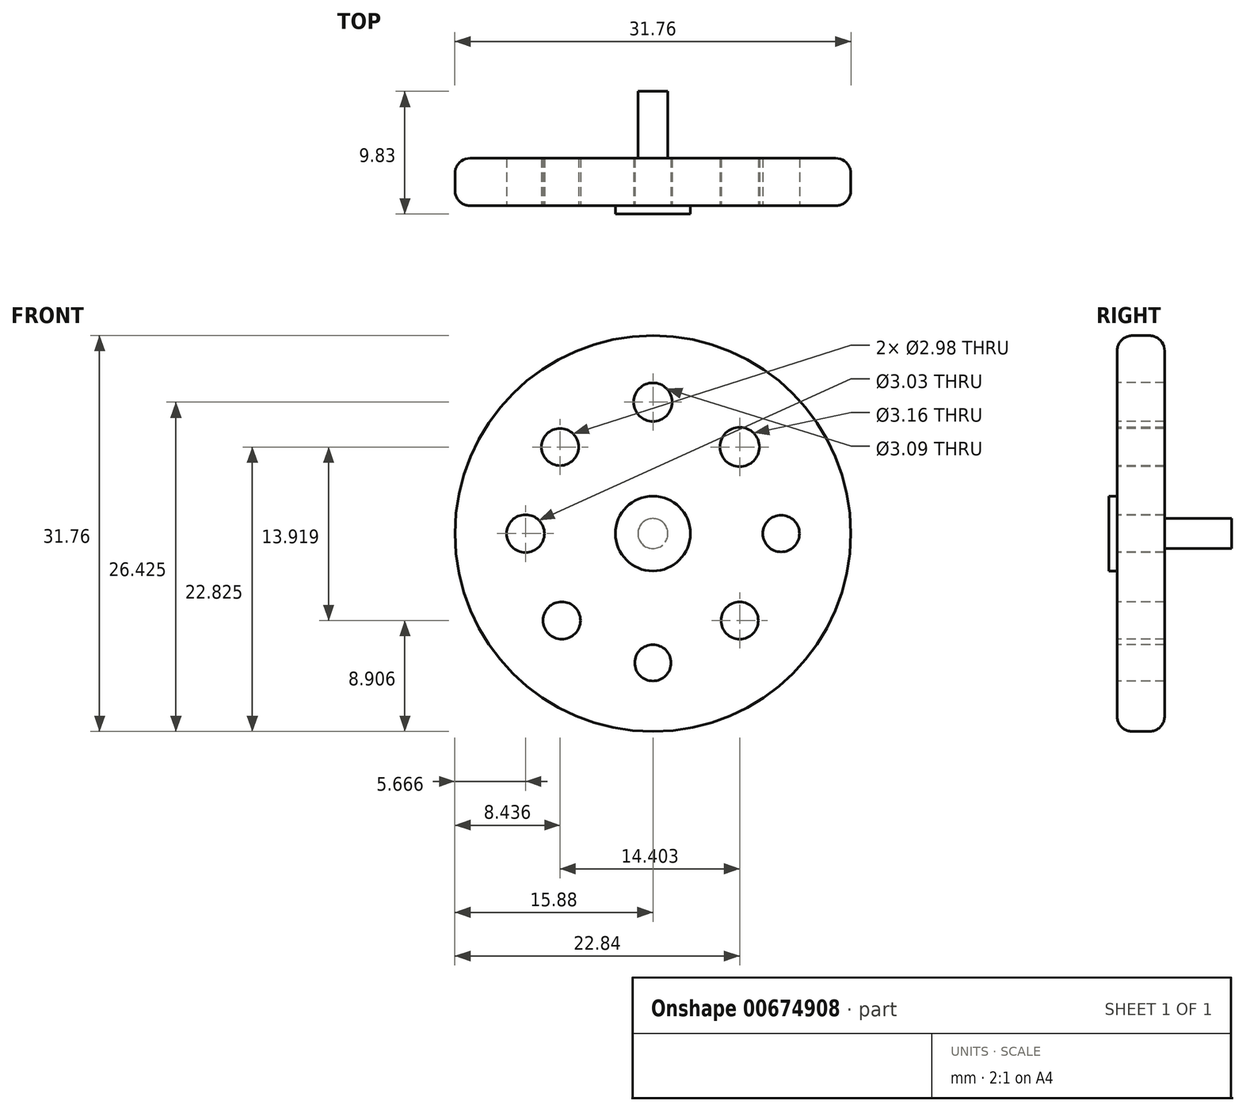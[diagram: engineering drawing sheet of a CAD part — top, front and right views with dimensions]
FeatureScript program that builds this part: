
annotation { "Feature Type Name" : "Feature", "Feature Type Description" : "" }
export const myFeature = defineFeature(function(context is Context, id is Id, definition is map)
    precondition{}
    {
        {
            var Q0;
            Q0=qCreatedBy(makeId("Front.planeOp"),FACE);
            var sketch = newSketch(context, id + "F0", { "sketchPlane" : qUnion([Q0])});
            skCircle(sketch, "E0", {"center": v(0, 0) * mm, "radius": 15.88 * mm});
            skSolve(sketch);
        }
        {
            var Q0;
            Q0=makeQuery(id+"F0.imprint","IMPRINT",FACE,{"disambiguationData":[TD([[makeQuery(id+"F0.imprint","IMPRINT",EDGE,{"derivedFrom":sQuery(id+"F0.wireOp",EDGE,"E0")}),1.0]])]});
            extrude(context, id + "F1", {"entities" : qUnion([Q0]), "depth" : 3.8 * mm, "offsetDistance" : 25.4 * mm});
        }
        {
            var Q0;
            Q0=makeQuery(id+"F1.opExtrude","CAP_FACE",FACE,{"disambiguationData":[OSD([sQuery(id+"F0.wireOp",EDGE,"E0")])],"isStart":false});
            var sketch = newSketch(context, id + "F2", { "sketchPlane" : qUnion([Q0])});
            skCircle(sketch, "E1", {"center": v(0, 0) * mm, "radius": 12.7 * mm});
            skSolve(sketch);
        }
        {
            var Q0;
            Q0=makeQuery(id+"F2.imprint","IMPRINT",FACE,{"disambiguationData":[TD([[makeQuery(id+"F2.imprint","IMPRINT",EDGE,{"derivedFrom":sQuery(id+"F2.wireOp",EDGE,"E1")}),1.0]])]});
            var sketch = newSketch(context, id + "F3", { "sketchPlane" : qUnion([Q0])});
            skCircle(sketch, "E2", {"center": v(0, 10.55) * mm, "radius": 1.54 * mm});
            skCircle(sketch, "E3", {"center": v(-10.21, 0) * mm, "radius": 1.51 * mm});
            skCircle(sketch, "E4", {"center": v(10.28, 0) * mm, "radius": 1.47 * mm});
            skCircle(sketch, "E5", {"center": v(0, -10.37) * mm, "radius": 1.45 * mm});
            skCircle(sketch, "E6", {"center": v(-7.44, 6.94) * mm, "radius": 1.5 * mm});
            skCircle(sketch, "E7", {"center": v(6.96, 6.94) * mm, "radius": 1.58 * mm});
            skCircle(sketch, "E8", {"center": v(-7.3, -6.97) * mm, "radius": 1.5 * mm});
            skCircle(sketch, "E9", {"center": v(6.96, -6.97) * mm, "radius": 1.5 * mm});
            skSolve(sketch);
        }
        {
            var Q0;
            Q0=makeQuery(id+"F3.imprint","IMPRINT",FACE,{"disambiguationData":[TD([[makeQuery(id+"F3.imprint","IMPRINT",EDGE,{"derivedFrom":sQuery(id+"F3.wireOp",EDGE,"E5")}),1.0]])]});
            var Q1;
            Q1=makeQuery(id+"F3.imprint","IMPRINT",FACE,{"disambiguationData":[TD([[makeQuery(id+"F3.imprint","IMPRINT",EDGE,{"derivedFrom":sQuery(id+"F3.wireOp",EDGE,"E8")}),1.0]])]});
            var Q2;
            Q2=makeQuery(id+"F3.imprint","IMPRINT",FACE,{"disambiguationData":[TD([[makeQuery(id+"F3.imprint","IMPRINT",EDGE,{"derivedFrom":sQuery(id+"F3.wireOp",EDGE,"E3")}),1.0]])]});
            var Q3;
            Q3=makeQuery(id+"F3.imprint","IMPRINT",FACE,{"disambiguationData":[TD([[makeQuery(id+"F3.imprint","IMPRINT",EDGE,{"derivedFrom":sQuery(id+"F3.wireOp",EDGE,"E6")}),1.0]])]});
            var Q4;
            Q4=makeQuery(id+"F3.imprint","IMPRINT",FACE,{"disambiguationData":[TD([[makeQuery(id+"F3.imprint","IMPRINT",EDGE,{"derivedFrom":sQuery(id+"F3.wireOp",EDGE,"E4")}),1.0]])]});
            var Q5;
            Q5=makeQuery(id+"F3.imprint","IMPRINT",FACE,{"disambiguationData":[TD([[makeQuery(id+"F3.imprint","IMPRINT",EDGE,{"derivedFrom":sQuery(id+"F3.wireOp",EDGE,"E9")}),1.0]])]});
            var Q6;
            Q6=makeQuery(id+"F3.imprint","IMPRINT",FACE,{"disambiguationData":[TD([[makeQuery(id+"F3.imprint","IMPRINT",EDGE,{"derivedFrom":sQuery(id+"F3.wireOp",EDGE,"E7")}),1.0]])]});
            var Q7;
            Q7=makeQuery(id+"F3.imprint","IMPRINT",FACE,{"disambiguationData":[TD([[makeQuery(id+"F3.imprint","IMPRINT",EDGE,{"derivedFrom":sQuery(id+"F3.wireOp",EDGE,"E2")}),1.0]])]});
            extrude(context, id + "F4", {"entities" : qUnion([Q0, Q1, Q2, Q3, Q4, Q5, Q6, Q7]), "operationType" : NewBodyOperationType.REMOVE, "oppositeDirection" : true, "depth" : 25.4 * mm, "offsetDistance" : 25.4 * mm});
        }
        {
            var Q0;
            Q0=makeQuery(id+"F2.imprint","IMPRINT",FACE,{"disambiguationData":[TD([[makeQuery(id+"F2.imprint","IMPRINT",EDGE,{"derivedFrom":sQuery(id+"F2.wireOp",EDGE,"E1")}),1.0]])]});
            var sketch = newSketch(context, id + "F5", { "sketchPlane" : qUnion([Q0])});
            skCircle(sketch, "E10", {"center": v(0, 0) * mm, "radius": 3 * mm});
            skSolve(sketch);
        }
        {
            var Q0;
            Q0=makeQuery(id+"F1.opExtrude","SWEPT_FACE",FACE,{"disambiguationData":[OSD([sQuery(id+"F0.wireOp",EDGE,"E0")])]});
            fillet(context, id + "F6", {"entities" : qUnion([Q0]), "radius" : 1.23 * mm, "tangentPropagation" : true, "allowEdgeOverflow" : false});
        }
        {
            var Q0;
            Q0=makeQuery(id+"F1.opExtrude","CAP_FACE",FACE,{"disambiguationData":[OSD([sQuery(id+"F0.wireOp",EDGE,"E0")])],"isStart":true});
            var sketch = newSketch(context, id + "F7", { "sketchPlane" : qUnion([Q0])});
            skCircle(sketch, "E11", {"center": v(0, 0) * mm, "radius": 1.2 * mm});
            skSolve(sketch);
        }
        {
            var Q0;
            Q0=makeQuery(id+"F7.imprint","IMPRINT",FACE,{"disambiguationData":[TD([[makeQuery(id+"F7.imprint","IMPRINT",EDGE,{"derivedFrom":sQuery(id+"F7.wireOp",EDGE,"E11")}),1.0]])]});
            extrude(context, id + "F8", {"entities" : qUnion([Q0]), "operationType" : NewBodyOperationType.ADD, "depth" : 5.36 * mm, "offsetDistance" : 25.4 * mm});
        }
        {
            var Q0;
            Q0=makeQuery(id+"F5.imprint","IMPRINT",FACE,{"disambiguationData":[TD([[makeQuery(id+"F5.imprint","IMPRINT",EDGE,{"derivedFrom":sQuery(id+"F5.wireOp",EDGE,"E10")}),1.0]])]});
            extrude(context, id + "F9", {"entities" : qUnion([Q0]), "operationType" : NewBodyOperationType.ADD, "depth" : 0.66 * mm, "offsetDistance" : 25.4 * mm});
        }
    });
